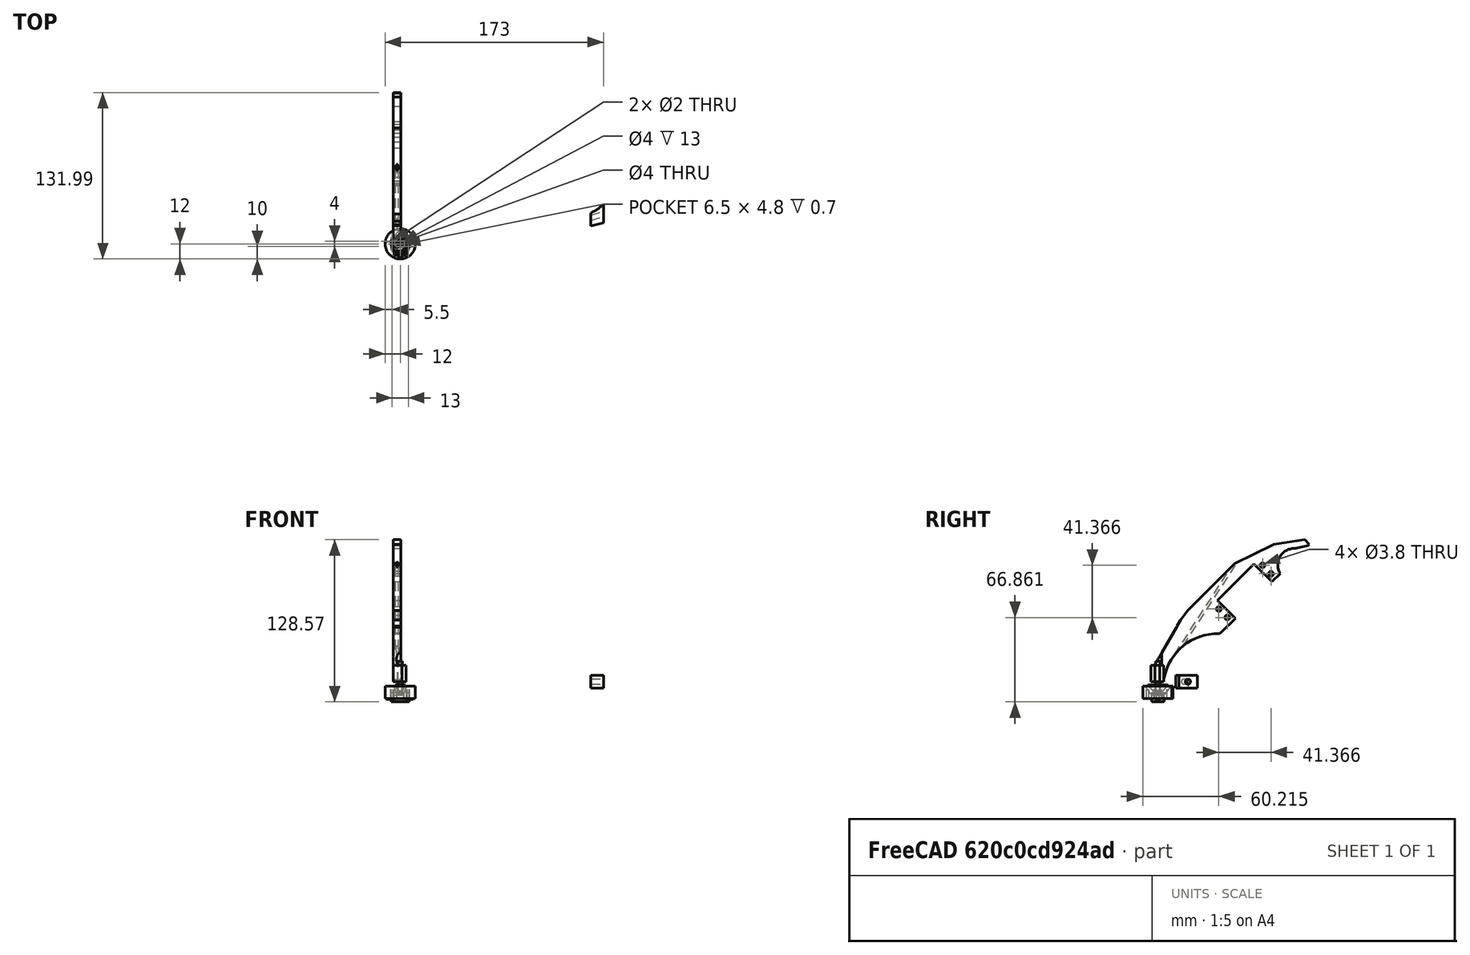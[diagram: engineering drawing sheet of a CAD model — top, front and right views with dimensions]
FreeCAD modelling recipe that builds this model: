
FCSTD DOCUMENT  (FreeCAD 0.16R6710 (Git))
Label: Feet sensor and leg 0.3
License: All rights reserved
LicenseURL: http://en.wikipedia.org/wiki/All_rights_reserved
objects: Part::Cut×37, Part::Cylinder×27, Part::Box×25, Part::Fuse×7, Part::Chamfer×4, Part::Sphere×3, Part::MultiCommon×2, Part::Cone×2, Part::FeaturePython×2, Part::Fillet×2, App::DocumentObjectGroup×1
note: 111 computed .brp shape members not serialized (recipe doc carries the construction recipe); baked Part::Feature solids carry a one-line shape summary decoded from their .brp

FEATURE [Part::Sphere] Sphere
  Angle1 = -90
  Angle2 = 90
  Angle3 = 360
  Radius = 3
FEATURE [Part::Cylinder] Cylinder
  Angle = 360
  Height = 10
  Radius = 1.5
FEATURE [Part::Box] Box  label="Cube"
  Height = 1
  Length = 6.5
  Placement = pos=(-3.25,-2.4,-4.2) rot=(0,0,1;0rad)
  Width = 4.8
FEATURE [Part::Cylinder] Cylinder001
  Angle = 360
  Height = 10
  Placement = pos=(-11,2,-3.7) rot=(0,1,0;1.5708rad)
  Radius = 0.25
FEATURE [Part::Cylinder] Cylinder002
  Angle = 360
  Height = 10
  Placement = pos=(0,-2,-3.7) rot=(0,1,0;1.5708rad)
  Radius = 0.25
FEATURE [Part::Box] Box001  label="Cube001"
  Height = 7.25
  Length = 14
  Placement = pos=(-7,-5,-6) rot=(0,0,1;0rad)
  Width = 10
FEATURE [Part::Box] Box002  label="Cube002"
  Height = 1
  Length = 6.5
  Placement = pos=(-3.25,-2.4,-4.2) rot=(0,0,1;0rad)
  Width = 4.8
FEATURE [Part::Cylinder] Cylinder003
  Angle = 360
  Height = 10
  Placement = pos=(-11,2,-3.7) rot=(0,1,0;1.5708rad)
  Radius = 0.25
FEATURE [Part::Cylinder] Cylinder004
  Angle = 360
  Height = 10
  Placement = pos=(0,-2,-3.7) rot=(0,1,0;1.5708rad)
  Radius = 0.25
FEATURE [Part::Fuse] Fusion
  Base = -> Cylinder003
  Tool = -> Cylinder004
FEATURE [Part::Fuse] Fusion001
  Base = -> Box002
  Tool = -> Fusion
FEATURE [Part::Box] Box003  label="Cube003"
  Height = 3
  Length = 10
  Placement = pos=(-5,-6,-3.5) rot=(0,0,1;0rad)
  Width = 12
FEATURE [Part::Cut] Cut
  Base = -> Box001
  Tool = -> Box003
FEATURE [Part::Cut] Cut001
  Base = -> Cut
  Tool = -> Fusion001
FEATURE [Part::Fuse] Fusion002
  Base = -> Cylinder001
  Tool = -> Cylinder002
FEATURE [Part::Fuse] Fusion003  label="Switch"
  Base = -> Box
  Tool = -> Fusion002
FEATURE [Part::Box] Box004  label="Cube004"
  Height = 5
  Length = 10
  Placement = pos=(-5,4,-3.55) rot=(0,0,1;0rad)
  Width = 3
FEATURE [Part::Sphere] Sphere001
  Angle1 = -90
  Angle2 = 90
  Angle3 = 360
  Radius = 3.1
FEATURE [Part::Cylinder] Cylinder005
  Angle = 360
  Height = 10
  Placement = pos=(0,0,0.5) rot=(0,0,1;0rad)
  Radius = 2.5
FEATURE [Part::Fuse] Fusion004
  Base = -> Sphere001
  Tool = -> Cylinder005
FEATURE [Part::Cut] Cut002
  Base = -> Cut001
  Tool = -> Fusion004
FEATURE [Part::Fuse] Fusion005  label="Ball and Screw"
  Base = -> Sphere
  Placement = pos=(0,0,-1) rot=(0,0,1;0rad)
  Tool = -> Cylinder
FEATURE [Part::Cut] Cut003
  Base = -> Cut001
  Tool = -> Fusion004
FEATURE [Part::Box] Box005  label="Cube005"
  Height = 8
  Length = 21
  Placement = pos=(-9,-7,-3.5) rot=(0,0,1;0rad)
  Width = 17
FEATURE [Part::Box] Box006  label="Cube006"
  Height = 12
  Length = 21
  Placement = pos=(-9,-7,-3.5) rot=(0,0,1;0rad)
  Width = 17
FEATURE [Part::Cut] Cut004  label="Bottom Switch holder"
  Base = -> Cut003
  Tool = -> Box005
FEATURE [Part::MultiCommon] Common  label="Ball and screw holder"
  Shapes = -> [Cut002,Box006]
FEATURE [Part::Cylinder] Cylinder006
  Angle = 360
  Height = 10
  Placement = pos=(0,0,-3.5) rot=(0,0,1;0rad)
  Radius = 12
FEATURE [Part::Box] Box007  label="Cube007"
  Height = 10
  Length = 10
  Placement = pos=(-5,-9,-3.5) rot=(0,0,1;0rad)
  Width = 20
FEATURE [Part::Cylinder] Cylinder007
  Angle = 360
  Height = 10
  Placement = pos=(0,0,-3.5) rot=(0,0,1;0rad)
  Radius = 7.1
FEATURE [Part::Cylinder] Cylinder008
  Angle = 360
  Height = 10
  Placement = pos=(0,0,-6.5) rot=(0,0,1;0rad)
  Radius = 7.1
FEATURE [Part::MultiCommon] Common002  label="Switch plate"
  Shapes = -> [Cut004,Cylinder008]
FEATURE [Part::Cylinder] Cylinder009
  Angle = 360
  Height = 13
  Placement = pos=(-6.5,2,-4) rot=(0,0,1;0rad)
  Radius = 1
FEATURE [Part::Cylinder] Cylinder010
  Angle = 360
  Height = 13
  Placement = pos=(6.5,-2,-4) rot=(0,0,1;0rad)
  Radius = 1
FEATURE [Part::Box] Box008  label="Cube008"
  Height = 12
  Length = 41
  Placement = pos=(42,14,-1) rot=(0,0,1;0rad)
  Width = 20
FEATURE [Part::Cylinder] Cylinder011
  Angle = 360
  Height = 12
  Placement = pos=(38,19.5,-1) rot=(0,0,1;0rad)
  Radius = 1.9
FEATURE [Part::Cylinder] Cylinder012
  Angle = 360
  Height = 12
  Placement = pos=(38,29,-1) rot=(0,0,1;0rad)
  Radius = 1.9
FEATURE [Part::Cylinder] Cylinder013
  Angle = 360
  Height = 12
  Placement = pos=(87,29,-1) rot=(0,0,1;0rad)
  Radius = 1.9
FEATURE [Part::Cylinder] Cylinder014
  Angle = 360
  Height = 12
  Placement = pos=(87,19.5,-1) rot=(0,0,1;0rad)
  Radius = 1.9
FEATURE [Part::Box] Box009  label="Cube009"
  Height = 6
  Length = 184
  Width = 34
FEATURE [Part::Box] Box010  label="Cube010"
  Height = 12
  Length = 37
  Width = 8
FEATURE [Part::Cylinder] Cylinder015
  Angle = 360
  Height = 10
  Placement = pos=(20,37,0) rot=(0,0,1;0rad)
  Radius = 13
FEATURE [Part::Cut] Cut008
  Base = -> Box009
  Tool = -> Box010
FEATURE [Part::Cut] Cut009
  Base = -> Cut008
  Tool = -> Cylinder015
FEATURE [Part::Cylinder] Cylinder016
  Angle = 360
  Height = 10
  Placement = pos=(132,63,0) rot=(0,0,1;0rad)
  Radius = 43
FEATURE [Part::Cut] Cut010
  Base = -> Cut009
  Tool = -> Cylinder016
FEATURE [Part::Box] Box011  label="Cube011"
  Height = 10
  Length = 41
  Placement = pos=(120,0,0) rot=(0,0,1;0rad)
  Width = 6
FEATURE [Part::Cut] Cut011
  Base = -> Cut010
  Tool = -> Box011
FEATURE [Part::Box] Box012  label="Cube012"
  Height = 10
  Length = 23
  Placement = pos=(161,0,0) rot=(0,0,1;0rad)
  Width = 17
FEATURE [Part::Cut] Cut012
  Base = -> Cut011
  Tool = -> Box012
FEATURE [Part::Box] Box013  label="Cube013"
  Height = 10
  Length = 13
  Placement = pos=(0,8,0) rot=(0,0,1;0rad)
  Width = 11
FEATURE [Part::Cut] Cut013
  Base = -> Cut012
  Tool = -> Box013
FEATURE [Part::Box] Box014  label="Cube014"
  Height = 10
  Length = 53
  Placement = pos=(-16,28,0) rot=(0,0,-1;0.628319rad)
  Width = 10
FEATURE [Part::Cut] Cut014
  Base = -> Cut013
  Tool = -> Box014
FEATURE [Part::Box] Box015  label="Cube015"
  Height = 10
  Length = 49
  Placement = pos=(16,5,0) rot=(0,0,-1;0.331613rad)
  Width = 10
FEATURE [Part::Cut] Cut015
  Base = -> Cut014
  Tool = -> Box015
FEATURE [Part::Box] Box016  label="Cube016"
  Height = 10
  Length = 76
  Placement = pos=(46,-7,0) rot=(0,0,1;0rad)
  Width = 10
FEATURE [Part::Cut] Cut016
  Base = -> Cut015
  Tool = -> Box016
FEATURE [Part::Box] Box017  label="Cube017"
  Height = 10
  Length = 65
  Placement = pos=(115,-7,0) rot=(0,0,1;0.261799rad)
  Width = 11
FEATURE [Part::Cut] Cut017
  Base = -> Cut016
  Tool = -> Box017
FEATURE [Part::Box] Box018  label="Cube018"
  Height = 10
  Length = 14
  Placement = pos=(174,10,0) rot=(0,0,1;0.279253rad)
  Width = 10
FEATURE [Part::Cut] Cut018
  Base = -> Cut017
  Tool = -> Box018
FEATURE [Part::Box] Box019  label="Cube019"
  Height = 10
  Length = 10
  Placement = pos=(106,-7,0) rot=(0,0,1;0.139626rad)
  Width = 10
FEATURE [Part::Cut] Cut019
  Base = -> Cut018
  Tool = -> Box019
FEATURE [Part::Cut] Cut020
  Base = -> Cut019
  Tool = -> Box008
FEATURE [Part::Cut] Cut021
  Base = -> Cut020
  Tool = -> Cylinder014
FEATURE [Part::Cut] Cut022
  Base = -> Cut021
  Tool = -> Cylinder013
FEATURE [Part::Cut] Cut023
  Base = -> Cut022
  Tool = -> Cylinder012
FEATURE [Part::Cut] Cut024
  Base = -> Cut023
  Tool = -> Cylinder011
FEATURE [Part::Chamfer] Chamfer
  Base = -> Cut024
  Edges = 1 edges r=6: [Edge36]
FEATURE [Part::Chamfer] Chamfer001
  Base = -> Chamfer
  Edges = 1 edges r=1: [Edge59]
FEATURE [Part::Box] Box020  label="Cube020"
  Height = 10
  Length = 10
  Placement = pos=(151,12,5) rot=(0,0,1;0rad)
  Width = 21
FEATURE [Part::Box] Box021  label="Cube021"
  Height = 13
  Length = 26
  Placement = pos=(161,15,-3) rot=(0,0,1;0rad)
  Width = 23
FEATURE [Part::Cut] Cut025
  Base = -> Chamfer001
  Placement = pos=(-5.5,-24,171) rot=(0,1,0;1.5708rad)
  Tool = -> Box021
FEATURE [Part::Cylinder] Cylinder017
  Angle = 360
  Height = 19
  Placement = pos=(132,63,0) rot=(0,0,1;0rad)
  Radius = 43
FEATURE [Part::Cut] Cut026
  Base = -> Box020
  Tool = -> Cylinder017
FEATURE [Part::Box] Box022  label="Cube022"
  Height = 20
  Length = 65
  Placement = pos=(115,-7,0) rot=(0,0,1;0.261799rad)
  Width = 11
FEATURE [Part::Cut] Cut027
  Base = -> Cut026
  Tool = -> Box022
FEATURE [Part::Cylinder] Cylinder018
  Angle = 360
  Height = 18
  Placement = pos=(146.076,19.1828,10) rot=(-0.146221,0.978386,0.146221;1.59265rad)
  Radius = 2
FEATURE [Part::Cut] Cut028
  Base = -> Cut027
  Tool = -> Cylinder018
FEATURE [Part::Cone] Cone
  Angle = 360
  Height = 7
  Placement = pos=(0,0,1) rot=(0,0,1;0rad)
  Radius1 = 3
  Radius2 = 5.5
FEATURE [Part::FeaturePython] Clone  label="Clone of Cone"  # Draft clone (typed FeaturePython)
  Objects = -> [Cone]
  Placement = pos=(0,0,0.5) rot=(0,0,1;0rad)
  Scale = (1,2,1)
FEATURE [Part::Box] Box023  label="Cube023"
  Height = 3.5
  Length = 10
  Placement = pos=(-5,-5,-4) rot=(0,0,1;0rad)
  Width = 10
FEATURE [Part::Cut] Cut029
  Base = -> Cylinder006
  Tool = -> Box023
FEATURE [Part::Cut] Cut030
  Base = -> Cut029
  Tool = -> Cylinder010
FEATURE [Part::Cut] Cut031
  Base = -> Cut030
  Tool = -> Cylinder009
FEATURE [Part::Cut] Cut032
  Base = -> Cut031
  Tool = -> Clone
FEATURE [Part::Cylinder] Cylinder019
  Angle = 360
  Height = 10
  Placement = pos=(0,0,-1) rot=(0,0,1;0rad)
  Radius = 1.5
FEATURE [Part::Cut] Cut033
  Base = -> Cut032
  Tool = -> Cylinder019
FEATURE [App::DocumentObjectGroup] Group  label="Not used"
  Group = -> [Box004,Common,Box007,Cylinder007,Cut028]
FEATURE [Part::Cone] Cone001
  Angle = 360
  Height = 6
  Placement = pos=(0,0,1) rot=(0,0,1;0rad)
  Radius1 = 2
  Radius2 = 4
FEATURE [Part::FeaturePython] Clone001  label="Clone of Cone001"  # Draft clone (typed FeaturePython)
  Objects = -> [Cone001]
  Placement = pos=(0,0,3) rot=(0,0,1;0rad)
  Scale = (1,2,0.75)
FEATURE [Part::Cylinder] Cylinder020
  Angle = 360
  Height = 16
  Placement = pos=(0,0,9) rot=(0,0,1;0rad)
  Radius = 2
FEATURE [Part::Sphere] Sphere002
  Angle1 = -90
  Angle2 = 90
  Angle3 = 360
  Placement = pos=(0,0,-1) rot=(0,0,1;0rad)
  Radius = 3
FEATURE [Part::Cut] Cut034  label="Foot"
  Base = -> Cut033
  Tool = -> Sphere002
FEATURE [Part::Cylinder] Cylinder021
  Angle = 360
  Height = 26
  Radius = 1.7
FEATURE [Part::Fillet] Fillet
  Base = -> Cut025
  Edges = 1 edges r=3: [Edge30]
FEATURE [Part::Cylinder] Cylinder022  label="Not used cylinder001"
  Angle = 360
  Height = 16
  Placement = pos=(0,-50,23) rot=(0,0,1;0rad)
  Radius = 3
FEATURE [Part::Fillet] Fillet001
  Base = -> Fillet
  Edges = 1 edges r=3: [Edge39]
FEATURE [Part::Box] Box024  label="Cube024"
  Height = 13
  Length = 10
  Placement = pos=(-5.5,-5.5,10) rot=(0,0,1;0rad)
  Width = 10
FEATURE [Part::Cut] Cut035
  Base = -> Fillet001
  Placement = pos=(0,-8,5) rot=(-1,0,0;0.785398rad)
  Tool = -> Cylinder022
FEATURE [Part::Cylinder] Cylinder023
  Angle = 360
  Height = 26
  Radius = 1.7
FEATURE [Part::Fuse] Fusion006
  Base = -> Box024
  Tool = -> Cut035
FEATURE [Part::Cylinder] Cylinder024
  Angle = 360
  Height = 16
  Placement = pos=(0,0,23) rot=(0,0,1;0rad)
  Radius = 3
FEATURE [Part::Cut] Cut036
  Base = -> Fusion006
  Tool = -> Cylinder024
FEATURE [Part::Cut] Cut037
  Base = -> Cut036
  Tool = -> Cylinder020
FEATURE [Part::Chamfer] Chamfer002
  Base = -> Cut037
  Edges = 1 edges r=3: [Edge13]
FEATURE [Part::Chamfer] Chamfer003
  Base = -> Chamfer002
  Edges = 1 edges r=3: [Edge21]
FEATURE [Part::Cylinder] Cylinder025
  Angle = 360
  Height = 96
  Placement = pos=(-2.5,14,31) rot=(-1,0,0;0.575959rad)
  Radius = 1
FEATURE [Part::Cut] Cut038  label="Leg"
  Base = -> Chamfer003
  Tool = -> Cylinder025
FEATURE [Part::Cylinder] Cylinder026
  Angle = 360
  Height = 16
  Placement = pos=(0,0,0.5) rot=(0,0,1;0rad)
  Radius = 2
FEATURE [Part::Cut] Cut039  label="Bottom of leg"
  Base = -> Clone001
  Tool = -> Cylinder026
